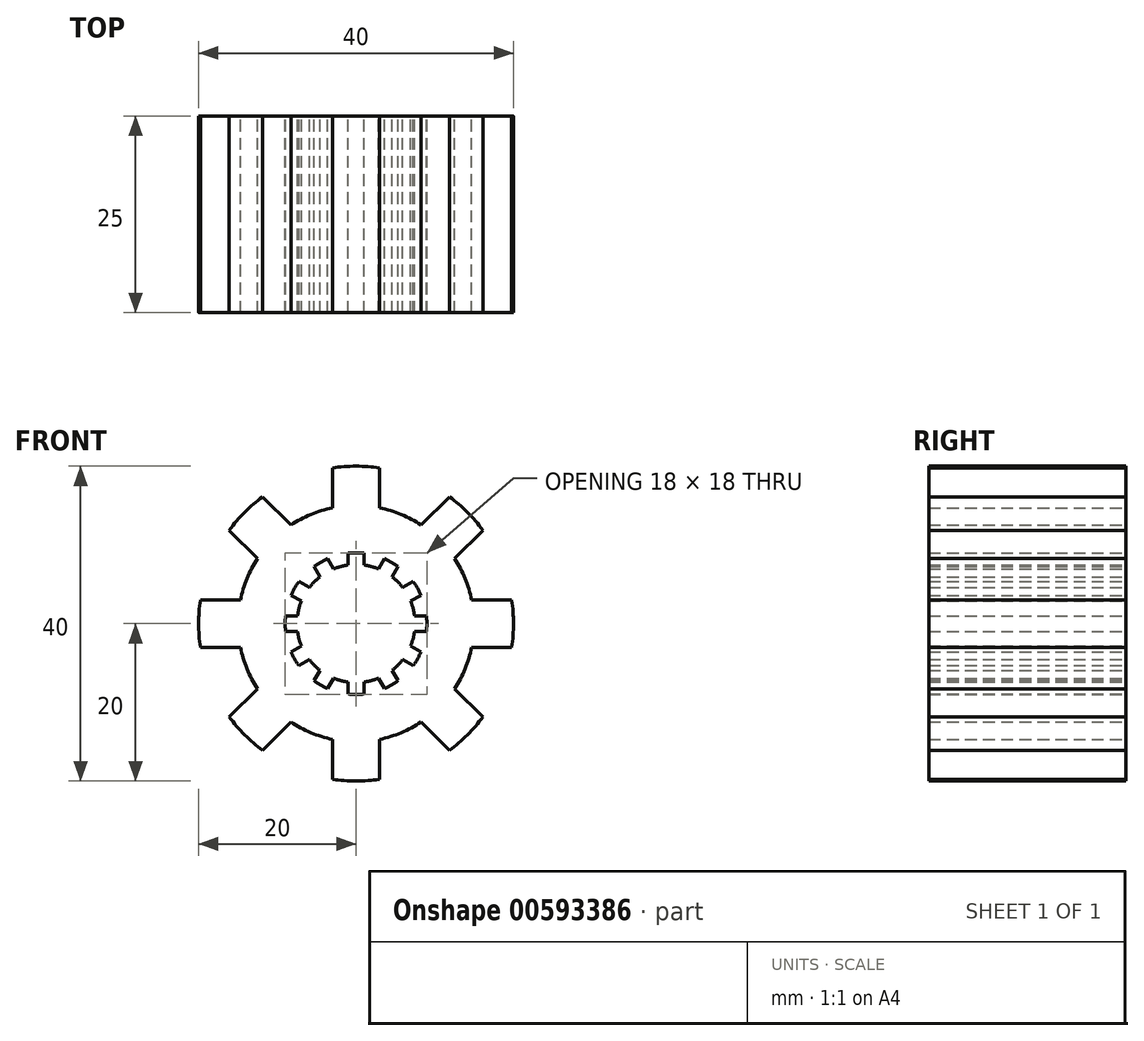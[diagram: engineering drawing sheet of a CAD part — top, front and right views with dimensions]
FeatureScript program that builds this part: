
annotation { "Feature Type Name" : "Feature", "Feature Type Description" : "" }
export const myFeature = defineFeature(function(context is Context, id is Id, definition is map)
    precondition{}
    {
        {
            var Q0;
            Q0=qCreatedBy(makeId("Front.planeOp"),FACE);
            var sketch = newSketch(context, id + "F0", { "sketchPlane" : qUnion([Q0])});
            skArc(sketch, "E0", {"start": v(-4.58, 5.94) * mm, "mid": v(-5.3, 5.3) * mm, "end": v(-5.94, 4.58) * mm});
            skArc(sketch, "E1", {"start": v(1, 8.94) * mm, "mid": v(0, 9) * mm, "end": v(-1, 8.94) * mm});
            skLineSegment(sketch, "E2", {"start": v(-1, 8.94) * mm, "end": v(-1, 7.43) * mm});
            skLineSegment(sketch, "E3", {"start": v(1, 7.43) * mm, "end": v(1, 8.94) * mm});
            skArc(sketch, "E4.1.0", {"start": v(-3.6, 8.25) * mm, "mid": v(-4.5, 7.8) * mm, "end": v(-5.34, 7.25) * mm});
            skLineSegment(sketch, "E4.1.1", {"start": v(-2.85, 6.94) * mm, "end": v(-3.6, 8.25) * mm});
            skLineSegment(sketch, "E4.1.2", {"start": v(-5.34, 7.25) * mm, "end": v(-4.58, 5.94) * mm});
            skArc(sketch, "E4.2.0", {"start": v(-7.25, 5.34) * mm, "mid": v(-7.8, 4.5) * mm, "end": v(-8.25, 3.6) * mm});
            skLineSegment(sketch, "E4.2.1", {"start": v(-5.94, 4.58) * mm, "end": v(-7.25, 5.34) * mm});
            skLineSegment(sketch, "E4.2.2", {"start": v(-8.25, 3.6) * mm, "end": v(-6.94, 2.85) * mm});
            skArc(sketch, "E4.3.0", {"start": v(-8.94, 1) * mm, "mid": v(-9, 0) * mm, "end": v(-8.94, -1) * mm});
            skLineSegment(sketch, "E4.3.1", {"start": v(-7.43, 1) * mm, "end": v(-8.94, 1) * mm});
            skLineSegment(sketch, "E4.3.2", {"start": v(-8.94, -1) * mm, "end": v(-7.43, -1) * mm});
            skArc(sketch, "E4.4.0", {"start": v(-8.25, -3.6) * mm, "mid": v(-7.8, -4.5) * mm, "end": v(-7.25, -5.34) * mm});
            skLineSegment(sketch, "E4.4.1", {"start": v(-6.94, -2.85) * mm, "end": v(-8.25, -3.6) * mm});
            skLineSegment(sketch, "E4.4.2", {"start": v(-7.25, -5.34) * mm, "end": v(-5.94, -4.58) * mm});
            skArc(sketch, "E4.5.0", {"start": v(-5.34, -7.25) * mm, "mid": v(-4.5, -7.8) * mm, "end": v(-3.6, -8.25) * mm});
            skLineSegment(sketch, "E4.5.1", {"start": v(-4.58, -5.94) * mm, "end": v(-5.34, -7.25) * mm});
            skLineSegment(sketch, "E4.5.2", {"start": v(-3.6, -8.25) * mm, "end": v(-2.85, -6.94) * mm});
            skArc(sketch, "E4.6.0", {"start": v(-1, -8.94) * mm, "mid": v(0, -9) * mm, "end": v(1, -8.94) * mm});
            skLineSegment(sketch, "E4.6.1", {"start": v(-1, -7.43) * mm, "end": v(-1, -8.94) * mm});
            skLineSegment(sketch, "E4.6.2", {"start": v(1, -8.94) * mm, "end": v(1, -7.43) * mm});
            skArc(sketch, "E4.7.0", {"start": v(3.6, -8.25) * mm, "mid": v(4.5, -7.8) * mm, "end": v(5.34, -7.25) * mm});
            skLineSegment(sketch, "E4.7.1", {"start": v(2.85, -6.94) * mm, "end": v(3.6, -8.25) * mm});
            skLineSegment(sketch, "E4.7.2", {"start": v(5.34, -7.25) * mm, "end": v(4.58, -5.94) * mm});
            skArc(sketch, "E4.8.0", {"start": v(7.25, -5.34) * mm, "mid": v(7.8, -4.5) * mm, "end": v(8.25, -3.6) * mm});
            skLineSegment(sketch, "E4.8.1", {"start": v(5.94, -4.58) * mm, "end": v(7.25, -5.34) * mm});
            skLineSegment(sketch, "E4.8.2", {"start": v(8.25, -3.6) * mm, "end": v(6.94, -2.85) * mm});
            skArc(sketch, "E4.9.0", {"start": v(8.94, -1) * mm, "mid": v(9, 0) * mm, "end": v(8.94, 1) * mm});
            skLineSegment(sketch, "E4.9.1", {"start": v(7.43, -1) * mm, "end": v(8.94, -1) * mm});
            skLineSegment(sketch, "E4.9.2", {"start": v(8.94, 1) * mm, "end": v(7.43, 1) * mm});
            skArc(sketch, "E4.10.0", {"start": v(8.25, 3.6) * mm, "mid": v(7.8, 4.5) * mm, "end": v(7.25, 5.34) * mm});
            skLineSegment(sketch, "E4.10.1", {"start": v(6.94, 2.85) * mm, "end": v(8.25, 3.6) * mm});
            skLineSegment(sketch, "E4.10.2", {"start": v(7.25, 5.34) * mm, "end": v(5.94, 4.58) * mm});
            skArc(sketch, "E4.11.0", {"start": v(5.34, 7.25) * mm, "mid": v(4.5, 7.8) * mm, "end": v(3.6, 8.25) * mm});
            skLineSegment(sketch, "E4.11.1", {"start": v(4.58, 5.94) * mm, "end": v(5.34, 7.25) * mm});
            skLineSegment(sketch, "E4.11.2", {"start": v(3.6, 8.25) * mm, "end": v(2.85, 6.94) * mm});
            skArc(sketch, "E5.trimOffspring", {"start": v(-1, 7.43) * mm, "mid": v(-1.94, 7.24) * mm, "end": v(-2.85, 6.94) * mm});
            skArc(sketch, "E6.trimOffspring", {"start": v(2.85, 6.94) * mm, "mid": v(1.94, 7.24) * mm, "end": v(1, 7.43) * mm});
            skArc(sketch, "E7.trimOffspring", {"start": v(5.94, 4.58) * mm, "mid": v(5.3, 5.3) * mm, "end": v(4.58, 5.94) * mm});
            skArc(sketch, "E8.trimOffspring", {"start": v(7.43, 1) * mm, "mid": v(7.24, 1.94) * mm, "end": v(6.94, 2.85) * mm});
            skArc(sketch, "E9.trimOffspring", {"start": v(6.94, -2.85) * mm, "mid": v(7.24, -1.94) * mm, "end": v(7.43, -1) * mm});
            skArc(sketch, "E10.trimOffspring", {"start": v(4.58, -5.94) * mm, "mid": v(5.3, -5.3) * mm, "end": v(5.94, -4.58) * mm});
            skArc(sketch, "E11.trimOffspring", {"start": v(1, -7.43) * mm, "mid": v(1.94, -7.24) * mm, "end": v(2.85, -6.94) * mm});
            skArc(sketch, "E12.trimOffspring", {"start": v(-2.85, -6.94) * mm, "mid": v(-1.94, -7.24) * mm, "end": v(-1, -7.43) * mm});
            skArc(sketch, "E13.trimOffspring", {"start": v(-5.94, -4.58) * mm, "mid": v(-5.3, -5.3) * mm, "end": v(-4.58, -5.94) * mm});
            skArc(sketch, "E14.trimOffspring", {"start": v(-7.43, -1) * mm, "mid": v(-7.24, -1.94) * mm, "end": v(-6.94, -2.85) * mm});
            skArc(sketch, "E15.trimOffspring", {"start": v(-6.94, 2.85) * mm, "mid": v(-7.24, 1.94) * mm, "end": v(-7.43, 1) * mm});
            skSolve(sketch);
        }
        {
            var Q0;
            Q0=qCreatedBy(makeId("Front.planeOp"),FACE);
            var sketch = newSketch(context, id + "F1", { "sketchPlane" : qUnion([Q0])});
            skCircle(sketch, "E16", {"center": v(0, 0) * mm, "radius": 15 * mm});
            skLineSegment(sketch, "E17", {"start": v(-3, 19.77) * mm, "end": v(-3, 14.7) * mm});
            skLineSegment(sketch, "E18", {"start": v(3, 14.7) * mm, "end": v(3, 19.77) * mm});
            skArc(sketch, "E19", {"start": v(3, 19.77) * mm, "mid": v(0, 20) * mm, "end": v(-3, 19.77) * mm});
            skArc(sketch, "E20.1.0", {"start": v(-11.86, 16.1) * mm, "mid": v(-14.14, 14.14) * mm, "end": v(-16.1, 11.86) * mm});
            skLineSegment(sketch, "E20.1.1", {"start": v(-8.27, 12.51) * mm, "end": v(-11.86, 16.1) * mm});
            skLineSegment(sketch, "E20.1.2", {"start": v(-16.1, 11.86) * mm, "end": v(-12.51, 8.27) * mm});
            skArc(sketch, "E20.2.0", {"start": v(-19.77, 3) * mm, "mid": v(-20, 0) * mm, "end": v(-19.77, -3) * mm});
            skLineSegment(sketch, "E20.2.1", {"start": v(-14.7, 3) * mm, "end": v(-19.77, 3) * mm});
            skLineSegment(sketch, "E20.2.2", {"start": v(-19.77, -3) * mm, "end": v(-14.7, -3) * mm});
            skArc(sketch, "E21.3.3.0", {"start": v(-16.1, -11.86) * mm, "mid": v(-14.14, -14.14) * mm, "end": v(-11.86, -16.1) * mm});
            skLineSegment(sketch, "E21.4.3.0", {"start": v(-12.51, -8.27) * mm, "end": v(-16.1, -11.86) * mm});
            skLineSegment(sketch, "E21.7.3.0", {"start": v(-11.86, -16.1) * mm, "end": v(-8.27, -12.51) * mm});
            skArc(sketch, "E21.3.4.0", {"start": v(-3, -19.77) * mm, "mid": v(0, -20) * mm, "end": v(3, -19.77) * mm});
            skLineSegment(sketch, "E21.4.4.0", {"start": v(-3, -14.7) * mm, "end": v(-3, -19.77) * mm});
            skLineSegment(sketch, "E21.7.4.0", {"start": v(3, -19.77) * mm, "end": v(3, -14.7) * mm});
            skArc(sketch, "E21.3.5.0", {"start": v(11.86, -16.1) * mm, "mid": v(14.14, -14.14) * mm, "end": v(16.1, -11.86) * mm});
            skLineSegment(sketch, "E21.4.5.0", {"start": v(8.27, -12.51) * mm, "end": v(11.86, -16.1) * mm});
            skLineSegment(sketch, "E21.7.5.0", {"start": v(16.1, -11.86) * mm, "end": v(12.51, -8.27) * mm});
            skArc(sketch, "E22.3.6.0", {"start": v(19.77, -3) * mm, "mid": v(20, 0) * mm, "end": v(19.77, 3) * mm});
            skLineSegment(sketch, "E22.4.6.0", {"start": v(14.7, -3) * mm, "end": v(19.77, -3) * mm});
            skLineSegment(sketch, "E22.7.6.0", {"start": v(19.77, 3) * mm, "end": v(14.7, 3) * mm});
            skArc(sketch, "E23.3.7.0", {"start": v(16.1, 11.86) * mm, "mid": v(14.14, 14.14) * mm, "end": v(11.86, 16.1) * mm});
            skLineSegment(sketch, "E23.4.7.0", {"start": v(12.51, 8.27) * mm, "end": v(16.1, 11.86) * mm});
            skLineSegment(sketch, "E23.7.7.0", {"start": v(11.86, 16.1) * mm, "end": v(8.27, 12.51) * mm});
            skSolve(sketch);
        }
        {
            var Q0;
            {var subQ0=sQuery(id+"F1.wireOp",EDGE,"E16");var subQ8=makeQuery(id+"F1.imprint","INTERSECT",VERTEX,{"derivedFrom":[subQ0,sQuery(id+"F1.wireOp",EDGE,"E22.7.6.0")]});Q0=makeQuery(id+"F1.imprint","IMPRINT",FACE,{"disambiguationData":[TD([[makeQuery(id+"F1.imprint","IMPRINT",EDGE,{"disambiguationData":[TD([[subQ8,-1.0]])],"derivedFrom":subQ0}),1.0]])]});}
            var Q1;
            Q1=makeQuery(id+"F1.imprint","IMPRINT",FACE,{"disambiguationData":[TD([[makeQuery(id+"F1.imprint","IMPRINT",EDGE,{"derivedFrom":sQuery(id+"F1.wireOp",EDGE,"E20.1.0")}),1.0]])]});
            var Q2;
            Q2=makeQuery(id+"F1.imprint","IMPRINT",FACE,{"disambiguationData":[TD([[makeQuery(id+"F1.imprint","IMPRINT",EDGE,{"derivedFrom":sQuery(id+"F1.wireOp",EDGE,"E20.2.0")}),1.0]])]});
            var Q3;
            Q3=makeQuery(id+"F1.imprint","IMPRINT",FACE,{"disambiguationData":[TD([[makeQuery(id+"F1.imprint","IMPRINT",EDGE,{"derivedFrom":sQuery(id+"F1.wireOp",EDGE,"E21.3.3.0")}),1.0]])]});
            var Q4;
            Q4=makeQuery(id+"F1.imprint","IMPRINT",FACE,{"disambiguationData":[TD([[makeQuery(id+"F1.imprint","IMPRINT",EDGE,{"derivedFrom":sQuery(id+"F1.wireOp",EDGE,"E21.3.4.0")}),1.0]])]});
            var Q5;
            Q5=makeQuery(id+"F1.imprint","IMPRINT",FACE,{"disambiguationData":[TD([[makeQuery(id+"F1.imprint","IMPRINT",EDGE,{"derivedFrom":sQuery(id+"F1.wireOp",EDGE,"E21.3.5.0")}),1.0]])]});
            var Q6;
            Q6=makeQuery(id+"F1.imprint","IMPRINT",FACE,{"disambiguationData":[TD([[makeQuery(id+"F1.imprint","IMPRINT",EDGE,{"derivedFrom":sQuery(id+"F1.wireOp",EDGE,"E22.3.6.0")}),1.0]])]});
            var Q7;
            Q7=makeQuery(id+"F1.imprint","IMPRINT",FACE,{"disambiguationData":[TD([[makeQuery(id+"F1.imprint","IMPRINT",EDGE,{"derivedFrom":sQuery(id+"F1.wireOp",EDGE,"E23.3.7.0")}),1.0]])]});
            var Q8;
            {var subQ0=sQuery(id+"F1.wireOp",EDGE,"E17");Q8=makeQuery(id+"F1.imprint","IMPRINT",FACE,{"disambiguationData":[TD([[makeQuery(id+"F1.imprint","IMPRINT",EDGE,{"derivedFrom":subQ0}),1.0]])]});}
            extrude(context, id + "F2", {"entities" : qUnion([Q0, Q1, Q2, Q3, Q4, Q5, Q6, Q7, Q8]), "depth" : 25 * mm, "offsetDistance" : 25 * mm});
        }
        {
            var Q0;
            Q0=makeQuery(id+"F0.imprint","IMPRINT",FACE,{"disambiguationData":[TD([[makeQuery(id+"F0.imprint","IMPRINT",EDGE,{"derivedFrom":sQuery(id+"F0.wireOp",EDGE,"E0")}),1.0]])]});
            extrude(context, id + "F3", {"entities" : qUnion([Q0]), "operationType" : NewBodyOperationType.REMOVE, "depth" : 25 * mm, "offsetDistance" : 25 * mm});
        }
    });
